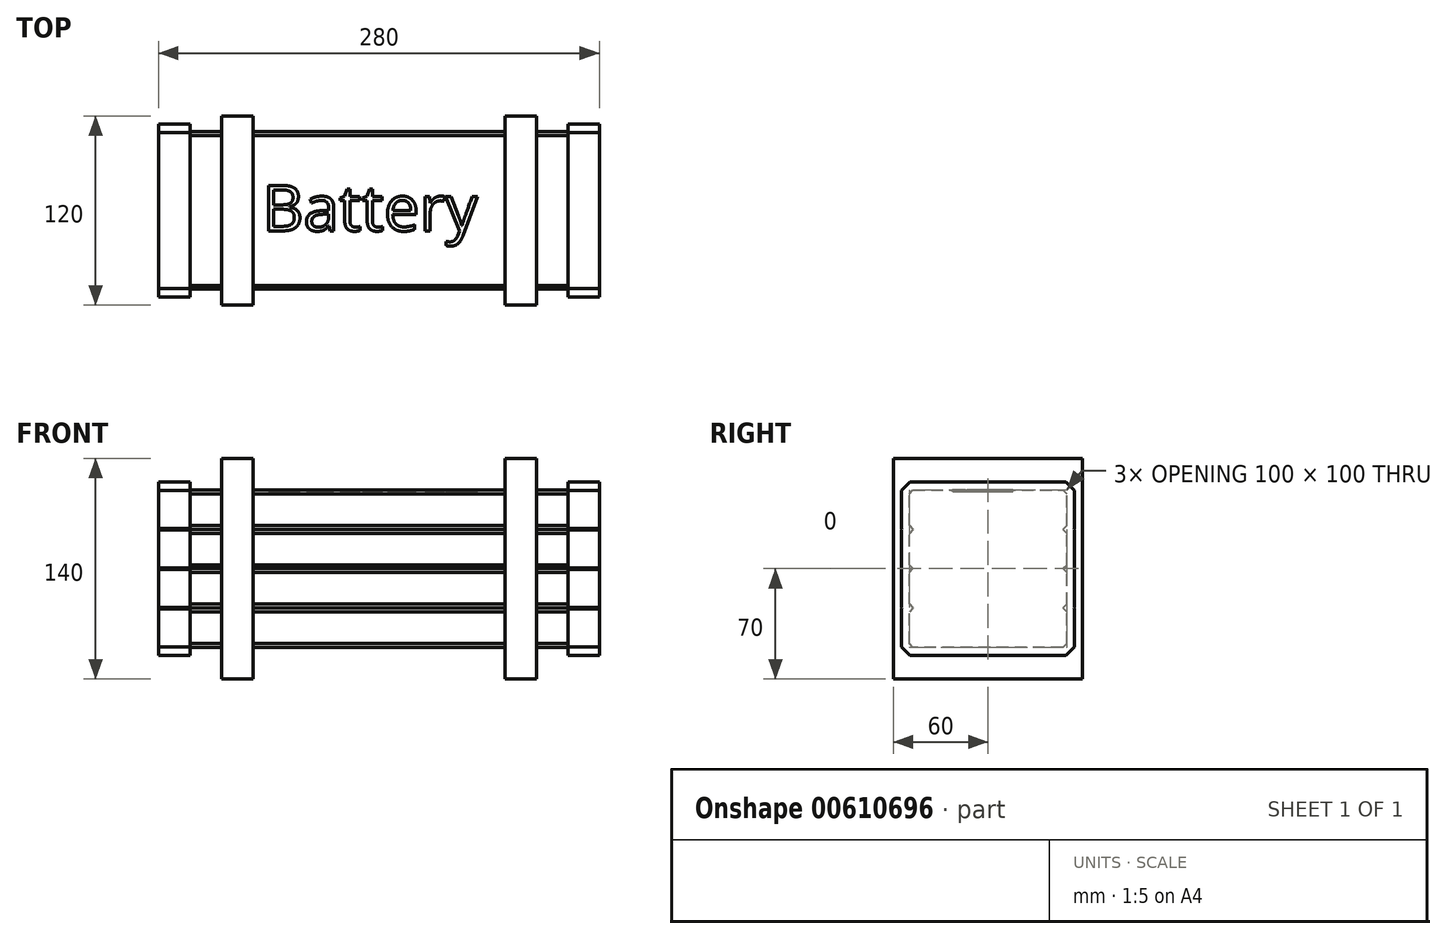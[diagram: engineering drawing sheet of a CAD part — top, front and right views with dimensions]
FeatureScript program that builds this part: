
annotation { "Feature Type Name" : "Feature", "Feature Type Description" : "" }
export const myFeature = defineFeature(function(context is Context, id is Id, definition is map)
    precondition{}
    {
        {
            var Q0;
            Q0=qCreatedBy(makeId("Top.planeOp"),FACE);
            var sketch = newSketch(context, id + "F0", { "sketchPlane" : qUnion([Q0])});
            skLineSegment(sketch, "E0.bottom", {"start": v(0, 0) * mm, "end": v(80, 0) * mm});
            skLineSegment(sketch, "E0.top", {"start": v(0, 100) * mm, "end": v(80, 100) * mm});
            skLineSegment(sketch, "E0.left", {"start": v(0, 0) * mm, "end": v(0, 100) * mm});
            skLineSegment(sketch, "E0.right", {"start": v(80, 0) * mm, "end": v(80, 100) * mm});
            skSolve(sketch);
        }
        {
            var Q0;
            Q0 = qSketchRegion(id + "F0", true);
            extrude(context, id + "F1", {"entities" : qUnion([Q0]), "depth" : 25 * mm, "offsetDistance" : 25 * mm});
        }
        {
            var Q0;
            Q0=makeQuery(id+"F1.opExtrude","CAP_EDGE",EDGE,{"disambiguationData":[OSD([sQuery(id+"F0.wireOp",EDGE,"E0.bottom")])],"isStart":false});
            var Q1;
            Q1=makeQuery(id+"F1.opExtrude","CAP_EDGE",EDGE,{"disambiguationData":[OSD([sQuery(id+"F0.wireOp",EDGE,"E0.bottom")])],"isStart":true});
            var Q2;
            Q2=makeQuery(id+"F1.opExtrude","CAP_EDGE",EDGE,{"disambiguationData":[OSD([sQuery(id+"F0.wireOp",EDGE,"E0.top")])],"isStart":false});
            var Q3;
            Q3=makeQuery(id+"F1.opExtrude","CAP_EDGE",EDGE,{"disambiguationData":[OSD([sQuery(id+"F0.wireOp",EDGE,"E0.top")])],"isStart":true});
            chamfer(context, id + "F2", {"entities" : qUnion([Q0, Q1, Q2, Q3]), "width" : 2.5 * mm, "tangentPropagation" : true});
        }
        {
            var Q0;
            Q0=makeQuery(id+"F1.opExtrude","SWEPT_BODY",BODY,{"disambiguationData":[OSD([sQuery(id+"F0.wireOp",EDGE,"E0.bottom"),sQuery(id+"F0.wireOp",EDGE,"E0.top"),sQuery(id+"F0.wireOp",EDGE,"E0.left"),sQuery(id+"F0.wireOp",EDGE,"E0.right")])]});
            var Q1;
            Q1=makeQuery(id+"F1.opExtrude","CAP_FACE",FACE,{"disambiguationData":[OSD([sQuery(id+"F0.wireOp",EDGE,"E0.bottom"),sQuery(id+"F0.wireOp",EDGE,"E0.top"),sQuery(id+"F0.wireOp",EDGE,"E0.left"),sQuery(id+"F0.wireOp",EDGE,"E0.right")])],"isStart":false});
            mirror(context, id + "F3", {"operationType" : NewBodyOperationType.ADD, "entities" : qUnion([Q0]), "mirrorPlane" : qUnion([Q1])});
        }
        {
            var Q0;
            Q0=makeQuery(id+"F1.opExtrude","SWEPT_BODY",BODY,{"disambiguationData":[OSD([sQuery(id+"F0.wireOp",EDGE,"E0.bottom"),sQuery(id+"F0.wireOp",EDGE,"E0.top"),sQuery(id+"F0.wireOp",EDGE,"E0.left"),sQuery(id+"F0.wireOp",EDGE,"E0.right")])]});
            var Q1;
            Q1=makeQuery(id+"F3.opPattern","COPY",FACE,{"derivedFrom":makeQuery(id+"F1.opExtrude","CAP_FACE",FACE,{"disambiguationData":[OSD([sQuery(id+"F0.wireOp",EDGE,"E0.bottom"),sQuery(id+"F0.wireOp",EDGE,"E0.top"),sQuery(id+"F0.wireOp",EDGE,"E0.left"),sQuery(id+"F0.wireOp",EDGE,"E0.right")])],"isStart":true}),"instanceName":"1"});
            mirror(context, id + "F4", {"operationType" : NewBodyOperationType.ADD, "entities" : qUnion([Q0]), "mirrorPlane" : qUnion([Q1])});
        }
        {
            var Q0;
            {var subQ0=makeQuery(id+"F1.opExtrude","SWEPT_FACE",FACE,{"disambiguationData":[OSD([sQuery(id+"F0.wireOp",EDGE,"E0.right")])]});var subQ1=makeQuery(id+"F3.boolean.opBoolean","MERGE",FACE,{"derivedFrom":[subQ0,makeQuery(id+"F3.opPattern","COPY",FACE,{"derivedFrom":subQ0,"instanceName":"1"})]});Q0=makeQuery(id+"F4.boolean.opBoolean","MERGE",FACE,{"derivedFrom":[subQ1,makeQuery(id+"F4.opPattern","COPY",FACE,{"derivedFrom":subQ1,"instanceName":"1"})]});}
            var sketch = newSketch(context, id + "F5", { "sketchPlane" : qUnion([Q0])});
            skLineSegment(sketch, "E1.bottom", {"start": v(-10, 120) * mm, "end": v(110, 120) * mm});
            skLineSegment(sketch, "E1.top", {"start": v(-10, -20) * mm, "end": v(110, -20) * mm});
            skLineSegment(sketch, "E1.left", {"start": v(-10, 120) * mm, "end": v(-10, -20) * mm});
            skLineSegment(sketch, "E1.right", {"start": v(110, 120) * mm, "end": v(110, -20) * mm});
            skSolve(sketch);
        }
        {
            var Q0;
            Q0=makeQuery(id+"F5.imprint","IMPRINT",FACE,{"disambiguationData":[TD([[makeQuery(id+"F5.imprint","IMPRINT",EDGE,{"derivedFrom":sQuery(id+"F5.wireOp",EDGE,"E1.bottom")}),-1.0]])]});
            var Q1;
            {var subQ0=sQuery(id+"F0.wireOp",EDGE,"E0.right");var subQ7=makeQuery(id+"F1.opExtrude","CAP_EDGE",EDGE,{"disambiguationData":[OSD([subQ0])],"isStart":true});Q1=makeQuery(id+"F5.imprint","IMPRINT",FACE,{"disambiguationData":[TD([[makeQuery(id+"F5.imprint","IMPRINT",EDGE,{"derivedFrom":subQ7}),1.0]])]});}
            extrude(context, id + "F6", {"entities" : qUnion([Q0, Q1]), "operationType" : NewBodyOperationType.ADD, "depth" : 10 * mm, "offsetDistance" : 25 * mm});
        }
        {
            var Q0;
            Q0=makeQuery(id+"F1.opExtrude","SWEPT_BODY",BODY,{"disambiguationData":[OSD([sQuery(id+"F0.wireOp",EDGE,"E0.bottom"),sQuery(id+"F0.wireOp",EDGE,"E0.top"),sQuery(id+"F0.wireOp",EDGE,"E0.left"),sQuery(id+"F0.wireOp",EDGE,"E0.right")])]});
            var Q1;
            {var subQ0=makeQuery(id+"F1.opExtrude","SWEPT_FACE",FACE,{"disambiguationData":[OSD([sQuery(id+"F0.wireOp",EDGE,"E0.left")])]});var subQ1=makeQuery(id+"F3.boolean.opBoolean","MERGE",FACE,{"derivedFrom":[subQ0,makeQuery(id+"F3.opPattern","COPY",FACE,{"derivedFrom":subQ0,"instanceName":"1"})]});Q1=makeQuery(id+"F4.boolean.opBoolean","MERGE",FACE,{"derivedFrom":[subQ1,makeQuery(id+"F4.opPattern","COPY",FACE,{"derivedFrom":subQ1,"instanceName":"1"})]});}
            mirror(context, id + "F7", {"operationType" : NewBodyOperationType.ADD, "entities" : qUnion([Q0]), "mirrorPlane" : qUnion([Q1])});
        }
        {
            var Q0;
            Q0=makeQuery(id+"F1.opExtrude","SWEPT_BODY",BODY,{"disambiguationData":[OSD([sQuery(id+"F0.wireOp",EDGE,"E0.bottom"),sQuery(id+"F0.wireOp",EDGE,"E0.top"),sQuery(id+"F0.wireOp",EDGE,"E0.left"),sQuery(id+"F0.wireOp",EDGE,"E0.right")])]});
            var Q1;
            Q1=makeQuery(id+"F6.opExtrude","CAP_FACE",FACE,{"disambiguationData":[OSD([sQuery(id+"F5.wireOp",EDGE,"E1.bottom"),sQuery(id+"F5.wireOp",EDGE,"E1.top"),sQuery(id+"F5.wireOp",EDGE,"E1.left"),sQuery(id+"F5.wireOp",EDGE,"E1.right")])],"isStart":false});
            mirror(context, id + "F8", {"operationType" : NewBodyOperationType.ADD, "entities" : qUnion([Q0]), "mirrorPlane" : qUnion([Q1])});
        }
        {
            var Q0;
            Q0=makeQuery(id+"F8.opPattern","COPY",FACE,{"derivedFrom":makeQuery(id+"F7.opPattern","COPY",FACE,{"derivedFrom":makeQuery(id+"F6.opExtrude","CAP_FACE",FACE,{"disambiguationData":[OSD([sQuery(id+"F5.wireOp",EDGE,"E1.bottom"),sQuery(id+"F5.wireOp",EDGE,"E1.top"),sQuery(id+"F5.wireOp",EDGE,"E1.left"),sQuery(id+"F5.wireOp",EDGE,"E1.right")])],"isStart":false}),"instanceName":"1"}),"instanceName":"1"});
            var sketch = newSketch(context, id + "F9", { "sketchPlane" : qUnion([Q0])});
            skLineSegment(sketch, "E2.bottom", {"start": v(-18.71, 121.56) * mm, "end": v(118.71, 121.56) * mm});
            skLineSegment(sketch, "E2.top", {"start": v(-18.71, -21.82) * mm, "end": v(118.71, -21.82) * mm});
            skLineSegment(sketch, "E2.left", {"start": v(-18.71, 121.56) * mm, "end": v(-18.71, -21.82) * mm});
            skLineSegment(sketch, "E2.right", {"start": v(118.71, 121.56) * mm, "end": v(118.71, -21.82) * mm});
            skSolve(sketch);
        }
        {
            var Q0;
            Q0 = qSketchRegion(id + "F9", true);
            extrude(context, id + "F10", {"entities" : qUnion([Q0]), "operationType" : NewBodyOperationType.REMOVE, "oppositeDirection" : true, "depth" : 150 * mm, "offsetDistance" : 25 * mm});
        }
        {
            var Q0;
            Q0=makeQuery(id+"F1.opExtrude","SWEPT_BODY",BODY,{"disambiguationData":[OSD([sQuery(id+"F0.wireOp",EDGE,"E0.bottom"),sQuery(id+"F0.wireOp",EDGE,"E0.top"),sQuery(id+"F0.wireOp",EDGE,"E0.left"),sQuery(id+"F0.wireOp",EDGE,"E0.right")])]});
            var Q1;
            Q1=makeQuery(id+"F7.opPattern","COPY",FACE,{"derivedFrom":makeQuery(id+"F6.opExtrude","CAP_FACE",FACE,{"disambiguationData":[OSD([sQuery(id+"F5.wireOp",EDGE,"E1.bottom"),sQuery(id+"F5.wireOp",EDGE,"E1.top"),sQuery(id+"F5.wireOp",EDGE,"E1.left"),sQuery(id+"F5.wireOp",EDGE,"E1.right")])],"isStart":false}),"instanceName":"1"});
            mirror(context, id + "F11", {"operationType" : NewBodyOperationType.ADD, "entities" : qUnion([Q0]), "mirrorPlane" : qUnion([Q1])});
        }
        {
            var Q0;
            Q0=makeQuery(id+"F11.opPattern","COPY",FACE,{"derivedFrom":makeQuery(id+"F10.boolean.opBoolean","COPY",FACE,{"derivedFrom":makeQuery(id+"F10.opExtrude","CAP_FACE",FACE,{"disambiguationData":[OSD([sQuery(id+"F9.wireOp",EDGE,"E2.bottom"),sQuery(id+"F9.wireOp",EDGE,"E2.top"),sQuery(id+"F9.wireOp",EDGE,"E2.left"),sQuery(id+"F9.wireOp",EDGE,"E2.right")])],"isStart":false})}),"instanceName":"1"});
            var sketch = newSketch(context, id + "F12", { "sketchPlane" : qUnion([Q0])});
            skLineSegment(sketch, "E3.bottom", {"start": v(-115.95, 124.22) * mm, "end": v(16.7, 124.22) * mm});
            skLineSegment(sketch, "E3.top", {"start": v(-115.95, -25.05) * mm, "end": v(16.7, -25.05) * mm});
            skLineSegment(sketch, "E3.left", {"start": v(-115.95, 124.22) * mm, "end": v(-115.95, -25.05) * mm});
            skLineSegment(sketch, "E3.right", {"start": v(16.7, 124.22) * mm, "end": v(16.7, -25.05) * mm});
            skSolve(sketch);
        }
        {
            var Q0;
            Q0 = qSketchRegion(id + "F12", true);
            extrude(context, id + "F13", {"entities" : qUnion([Q0]), "operationType" : NewBodyOperationType.REMOVE, "oppositeDirection" : true, "depth" : 180 * mm, "offsetDistance" : 25 * mm});
        }
        {
            var Q0;
            Q0=makeQuery(id+"F10.boolean.opBoolean","COPY",FACE,{"derivedFrom":makeQuery(id+"F10.opExtrude","CAP_FACE",FACE,{"disambiguationData":[OSD([sQuery(id+"F9.wireOp",EDGE,"E2.bottom"),sQuery(id+"F9.wireOp",EDGE,"E2.top"),sQuery(id+"F9.wireOp",EDGE,"E2.left"),sQuery(id+"F9.wireOp",EDGE,"E2.right")])],"isStart":false})});
            var sketch = newSketch(context, id + "F14", { "sketchPlane" : qUnion([Q0])});
            skLineSegment(sketch, "E4.0", {"start": v(105, 25.43) * mm, "end": v(104.57, 25) * mm});
            skLineSegment(sketch, "E4.1", {"start": v(104.57, 25) * mm, "end": v(105, 24.57) * mm});
            skLineSegment(sketch, "E4.2", {"start": v(105, 0.43) * mm, "end": v(105, 24.57) * mm});
            skLineSegment(sketch, "E4.3", {"start": v(-5, 99.57) * mm, "end": v(-5, 75.43) * mm});
            skLineSegment(sketch, "E4.4", {"start": v(-5, 99.57) * mm, "end": v(0.43, 105) * mm});
            skLineSegment(sketch, "E4.5", {"start": v(99.57, 105) * mm, "end": v(0.43, 105) * mm});
            skLineSegment(sketch, "E4.6", {"start": v(105, 99.57) * mm, "end": v(99.57, 105) * mm});
            skLineSegment(sketch, "E4.7", {"start": v(105, 75.43) * mm, "end": v(105, 99.57) * mm});
            skLineSegment(sketch, "E4.8", {"start": v(105, 75.43) * mm, "end": v(104.57, 75) * mm});
            skLineSegment(sketch, "E4.9", {"start": v(105, 49.57) * mm, "end": v(104.57, 50) * mm});
            skLineSegment(sketch, "E4.10", {"start": v(104.57, 50) * mm, "end": v(105, 50.43) * mm});
            skLineSegment(sketch, "E4.11", {"start": v(105, 50.43) * mm, "end": v(105, 74.57) * mm});
            skLineSegment(sketch, "E4.12", {"start": v(104.57, 75) * mm, "end": v(105, 74.57) * mm});
            skLineSegment(sketch, "E4.13", {"start": v(-5, 75.43) * mm, "end": v(-4.57, 75) * mm});
            skLineSegment(sketch, "E4.14", {"start": v(-4.57, 75) * mm, "end": v(-5, 74.57) * mm});
            skLineSegment(sketch, "E4.15", {"start": v(-5, 74.57) * mm, "end": v(-5, 50.43) * mm});
            skLineSegment(sketch, "E4.16", {"start": v(105, 25.43) * mm, "end": v(105, 49.57) * mm});
            skLineSegment(sketch, "E4.17", {"start": v(-4.57, 50) * mm, "end": v(-5, 50.43) * mm});
            skLineSegment(sketch, "E4.18", {"start": v(-5, 49.57) * mm, "end": v(-4.57, 50) * mm});
            skLineSegment(sketch, "E4.19", {"start": v(-5, 49.57) * mm, "end": v(-5, 25.43) * mm});
            skLineSegment(sketch, "E4.20", {"start": v(-5, 25.43) * mm, "end": v(-4.57, 25) * mm});
            skLineSegment(sketch, "E4.21", {"start": v(-4.57, 25) * mm, "end": v(-5, 24.57) * mm});
            skLineSegment(sketch, "E4.22", {"start": v(-5, 24.57) * mm, "end": v(-5, 0.43) * mm});
            skLineSegment(sketch, "E4.23", {"start": v(0.43, -5) * mm, "end": v(-5, 0.43) * mm});
            skLineSegment(sketch, "E4.24", {"start": v(0.43, -5) * mm, "end": v(99.57, -5) * mm});
            skLineSegment(sketch, "E4.25", {"start": v(99.57, -5) * mm, "end": v(105, 0.43) * mm});
            skSolve(sketch);
        }
        {
            var Q0;
            Q0=makeQuery(id+"F14.imprint","IMPRINT",FACE,{"disambiguationData":[TD([[makeQuery(id+"F14.imprint","IMPRINT",EDGE,{"derivedFrom":sQuery(id+"F14.wireOp",EDGE,"E4.0")}),-1.0]])]});
            var Q1;
            {var subQ0=makeQuery(id+"F10.opExtrude","CAP_FACE",FACE,{"disambiguationData":[OSD([sQuery(id+"F9.wireOp",EDGE,"E2.bottom"),sQuery(id+"F9.wireOp",EDGE,"E2.top"),sQuery(id+"F9.wireOp",EDGE,"E2.left"),sQuery(id+"F9.wireOp",EDGE,"E2.right")])],"isStart":false});var subQ1=sQuery(id+"F0.wireOp",EDGE,"E0.bottom");var subQ13=makeQuery(id+"F1.opExtrude","SWEPT_FACE",FACE,{"disambiguationData":[OSD([subQ1])]});Q1=makeQuery(id+"F14.imprint","IMPRINT",FACE,{"disambiguationData":[TD([[makeQuery(id+"F14.imprint","IMPRINT",EDGE,{"derivedFrom":makeQuery(id+"F10.boolean.opBoolean","INTERSECT",EDGE,{"derivedFrom":[makeQuery(id+"F8.opPattern","COPY",FACE,{"derivedFrom":makeQuery(id+"F7.boolean.opBoolean","MERGE",FACE,{"derivedFrom":[subQ13,makeQuery(id+"F7.opPattern","COPY",FACE,{"derivedFrom":subQ13,"instanceName":"1"})]}),"instanceName":"1"}),subQ0]})}),1.0]])]});}
            extrude(context, id + "F15", {"entities" : qUnion([Q0, Q1]), "operationType" : NewBodyOperationType.ADD, "depth" : 20 * mm, "offsetDistance" : 25 * mm});
        }
        {
            var Q0;
            Q0=makeQuery(id+"F13.boolean.opBoolean","COPY",FACE,{"derivedFrom":makeQuery(id+"F13.opExtrude","CAP_FACE",FACE,{"disambiguationData":[OSD([sQuery(id+"F12.wireOp",EDGE,"E3.bottom"),sQuery(id+"F12.wireOp",EDGE,"E3.top"),sQuery(id+"F12.wireOp",EDGE,"E3.left"),sQuery(id+"F12.wireOp",EDGE,"E3.right")])],"isStart":false})});
            var sketch = newSketch(context, id + "F16", { "sketchPlane" : qUnion([Q0])});
            skLineSegment(sketch, "E5.0", {"start": v(-105, 24.57) * mm, "end": v(-105, 0.43) * mm});
            skLineSegment(sketch, "E5.1", {"start": v(-105, 0.43) * mm, "end": v(-99.57, -5) * mm});
            skLineSegment(sketch, "E5.2", {"start": v(-99.57, -5) * mm, "end": v(-0.43, -5) * mm});
            skLineSegment(sketch, "E5.3", {"start": v(-0.43, 105) * mm, "end": v(-99.57, 105) * mm});
            skLineSegment(sketch, "E5.4", {"start": v(-99.57, 105) * mm, "end": v(-105, 99.57) * mm});
            skLineSegment(sketch, "E5.5", {"start": v(-105, 99.57) * mm, "end": v(-105, 75.43) * mm});
            skLineSegment(sketch, "E5.6", {"start": v(-104.57, 75) * mm, "end": v(-105, 75.43) * mm});
            skLineSegment(sketch, "E5.7", {"start": v(-105, 74.57) * mm, "end": v(-104.57, 75) * mm});
            skLineSegment(sketch, "E5.8", {"start": v(-105, 74.57) * mm, "end": v(-105, 50.43) * mm});
            skLineSegment(sketch, "E5.9", {"start": v(-104.57, 25) * mm, "end": v(-105, 25.43) * mm});
            skLineSegment(sketch, "E5.10", {"start": v(-105, 49.57) * mm, "end": v(-105, 25.43) * mm});
            skLineSegment(sketch, "E5.11", {"start": v(-104.57, 50) * mm, "end": v(-105, 49.57) * mm});
            skLineSegment(sketch, "E5.12", {"start": v(-105, 50.43) * mm, "end": v(-104.57, 50) * mm});
            skLineSegment(sketch, "E5.13", {"start": v(-0.43, 105) * mm, "end": v(5, 99.57) * mm});
            skLineSegment(sketch, "E5.14", {"start": v(5, 75.43) * mm, "end": v(5, 99.57) * mm});
            skLineSegment(sketch, "E5.15", {"start": v(4.57, 75) * mm, "end": v(5, 75.43) * mm});
            skLineSegment(sketch, "E5.16", {"start": v(-105, 24.57) * mm, "end": v(-104.57, 25) * mm});
            skLineSegment(sketch, "E5.17", {"start": v(5, 74.57) * mm, "end": v(4.57, 75) * mm});
            skLineSegment(sketch, "E5.18", {"start": v(5, 50.43) * mm, "end": v(5, 74.57) * mm});
            skLineSegment(sketch, "E5.19", {"start": v(5, 50.43) * mm, "end": v(4.57, 50) * mm});
            skLineSegment(sketch, "E5.20", {"start": v(4.57, 50) * mm, "end": v(5, 49.57) * mm});
            skLineSegment(sketch, "E5.21", {"start": v(5, 25.43) * mm, "end": v(5, 49.57) * mm});
            skLineSegment(sketch, "E5.22", {"start": v(4.57, 25) * mm, "end": v(5, 25.43) * mm});
            skLineSegment(sketch, "E5.23", {"start": v(5, 24.57) * mm, "end": v(4.57, 25) * mm});
            skLineSegment(sketch, "E5.24", {"start": v(5, 0.43) * mm, "end": v(5, 24.57) * mm});
            skLineSegment(sketch, "E5.25", {"start": v(5, 0.43) * mm, "end": v(-0.43, -5) * mm});
            skSolve(sketch);
        }
        {
            var Q0;
            Q0 = qSketchRegion(id + "F16", true);
            extrude(context, id + "F17", {"entities" : qUnion([Q0]), "operationType" : NewBodyOperationType.ADD, "depth" : 20 * mm, "offsetDistance" : 25 * mm});
        }
        {
            var Q0;
            {var subQ0=makeQuery(id+"F4.opPattern","COPY",FACE,{"derivedFrom":makeQuery(id+"F1.opExtrude","CAP_FACE",FACE,{"disambiguationData":[OSD([sQuery(id+"F0.wireOp",EDGE,"E0.bottom"),sQuery(id+"F0.wireOp",EDGE,"E0.top"),sQuery(id+"F0.wireOp",EDGE,"E0.left"),sQuery(id+"F0.wireOp",EDGE,"E0.right")])],"isStart":true}),"instanceName":"1"});Q0=makeQuery(id+"F7.boolean.opBoolean","MERGE",FACE,{"derivedFrom":[subQ0,makeQuery(id+"F7.opPattern","COPY",FACE,{"derivedFrom":subQ0,"instanceName":"1"})]});}
            var sketch = newSketch(context, id + "F18", { "sketchPlane" : qUnion([Q0])});
            skText(sketch, "E6", { "text": "Battery", "fontName": "OpenSans-Regular.ttf"});
            const initialGuessF18  = {"E6": [-0.07417, 0.0371, 1, 0, 0.02913]};
            skSetInitialGuess(sketch, initialGuessF18);
            skSolve(sketch);
        }
        {
            var Q0;
            Q0 = qSketchRegion(id + "F18", true);
            extrude(context, id + "F19", {"entities" : qUnion([Q0]), "operationType" : NewBodyOperationType.REMOVE, "oppositeDirection" : true, "depth" : 1 * mm, "offsetDistance" : 25 * mm});
        }
    });
